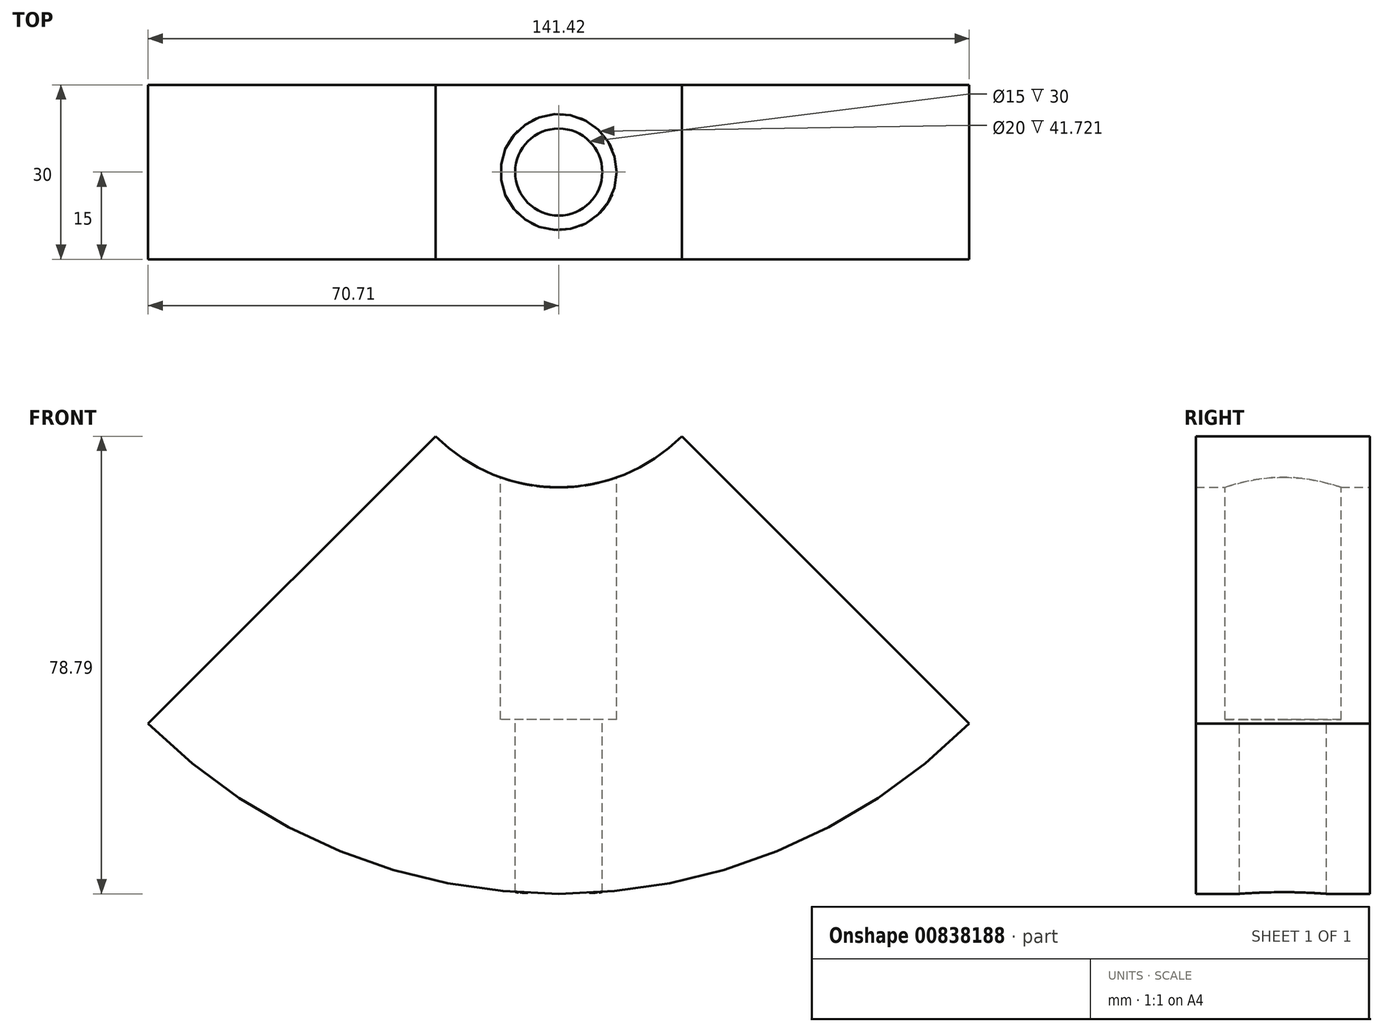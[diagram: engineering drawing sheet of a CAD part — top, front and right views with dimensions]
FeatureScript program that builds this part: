
annotation { "Feature Type Name" : "Feature", "Feature Type Description" : "" }
export const myFeature = defineFeature(function(context is Context, id is Id, definition is map)
    precondition{}
    {
        {
            var Q0;
            Q0=qCreatedBy(makeId("Front.planeOp"),FACE);
            var sketch = newSketch(context, id + "F0", { "sketchPlane" : qUnion([Q0])});
            skArc(sketch, "E0", {"start": v(-70.71, -70.71) * mm, "mid": v(0, -100) * mm, "end": v(70.71, -70.71) * mm});
            skLineSegment(sketch, "E1", {"start": v(0, -30) * mm, "end": v(0, -100) * mm});
            skLineSegment(sketch, "E2.3.0", {"start": v(-70.71, -70.71) * mm, "end": v(-21.21, -21.21) * mm});
            skLineSegment(sketch, "E2.4.0", {"start": v(0, -100) * mm, "end": v(0, -30) * mm});
            skLineSegment(sketch, "E2.5.0", {"start": v(70.71, -70.71) * mm, "end": v(21.21, -21.21) * mm});
            skPoint(sketch, "E3.orphan", {"position": v(0, 100) * mm});
            skPoint(sketch, "E4.orphan", {"position": v(100, 0) * mm});
            skPoint(sketch, "E5.orphan", {"position": v(70.71, 70.71) * mm});
            skLineSegment(sketch, "E6.trimOffspring", {"start": v(21.21, -21.21) * mm, "end": v(70.71, -70.71) * mm});
            skLineSegment(sketch, "E7.trimOffspring", {"start": v(-21.21, -21.21) * mm, "end": v(-70.71, -70.71) * mm});
            skArc(sketch, "E8.trimOffspring", {"start": v(-21.21, -21.21) * mm, "mid": v(0, -30) * mm, "end": v(21.21, -21.21) * mm});
            skSolve(sketch);
        }
        {
            var Q0;
            Q0=qSketchRegion(id+"F0",true);
            extrude(context, id + "F1", {"entities" : qUnion([Q0]), "endBound" : BoundingType.SYMMETRIC, "depth" : 30 * mm, "offsetDistance" : 25 * mm});
        }
        {
            var Q0;
            Q0=qCreatedBy(makeId("Top.planeOp"),FACE);
            var sketch = newSketch(context, id + "F2", { "sketchPlane" : qUnion([Q0])});
            skCircle(sketch, "E9", {"center": v(0, 0) * mm, "radius": 7.5 * mm});
            skSolve(sketch);
        }
        {
            var Q0;
            Q0 = qSketchRegion(id + "F2", true);
            extrude(context, id + "F3", {"entities" : qUnion([Q0]), "operationType" : NewBodyOperationType.REMOVE, "oppositeDirection" : true, "depth" : 105.45 * mm, "offsetDistance" : 25 * mm});
        }
        {
            var Q0;
            Q0=qCreatedBy(makeId("Top.planeOp"),FACE);
            var sketch = newSketch(context, id + "F4", { "sketchPlane" : qUnion([Q0])});
            skCircle(sketch, "E10", {"center": v(0, 0) * mm, "radius": 10 * mm});
            skSolve(sketch);
        }
        {
            var Q0;
            Q0 = qSketchRegion(id + "F4", true);
            extrude(context, id + "F5", {"entities" : qUnion([Q0]), "operationType" : NewBodyOperationType.REMOVE, "oppositeDirection" : true, "depth" : 70 * mm, "offsetDistance" : 25 * mm});
        }
    });
